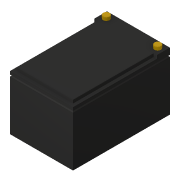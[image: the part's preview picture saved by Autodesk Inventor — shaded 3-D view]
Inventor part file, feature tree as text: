
AUTODESK INVENTOR PART (.ipt)
format: ipt  version: 2018.2 (Build 222227000, 227)  size: 715,776 bytes
history: native  units: mm
features: extrude x5, sketch x5, projected_geometry x1
ambient origin geometry x8: Origin, YZ Plane, XZ Plane, XY Plane, X Axis, Y Axis, Z Axis, Center Point
bodies: Volumenkörper1 (feature_tree)
feature tree (11):
  extrude  "Grundkörper"  Depth=151.0mm
  extrude  "Cap"  Depth=2.5mm TaperAngle=45.0deg
  extrude  "Absatz"  Depth=5.0mm
  extrude  "Connectors"  Depth=5.0mm TaperAngle=0.0deg
  extrude  "Schrift"  Depth=10.0mm
  sketch  "Skizze1"  dims[d0=98.0mm d1=151.0mm]
  sketch  "Skizze2"  dims[d2=83.0mm d3=0.0mm d4=2.5mm d5=2.0mm d6=45.0deg]
  sketch  "Skizze3"  dims[d7=10.0mm d8=0.0mm d9=5.0mm]
  sketch  "Skizze4"  dims[d10=5.0mm d11=5.0mm d12=0.0mm]
  sketch  "Skizze5"  dims[d13=20.0mm d14=10.0mm d15=80.0mm d16=5.0mm d17=0.0mm d18=10.0mm d19=10.0mm d20=30.0mm d21=5.0mm d22=0.5mm d23=0.0mm]
  projected_geometry  "Projizierte Kontur1"
